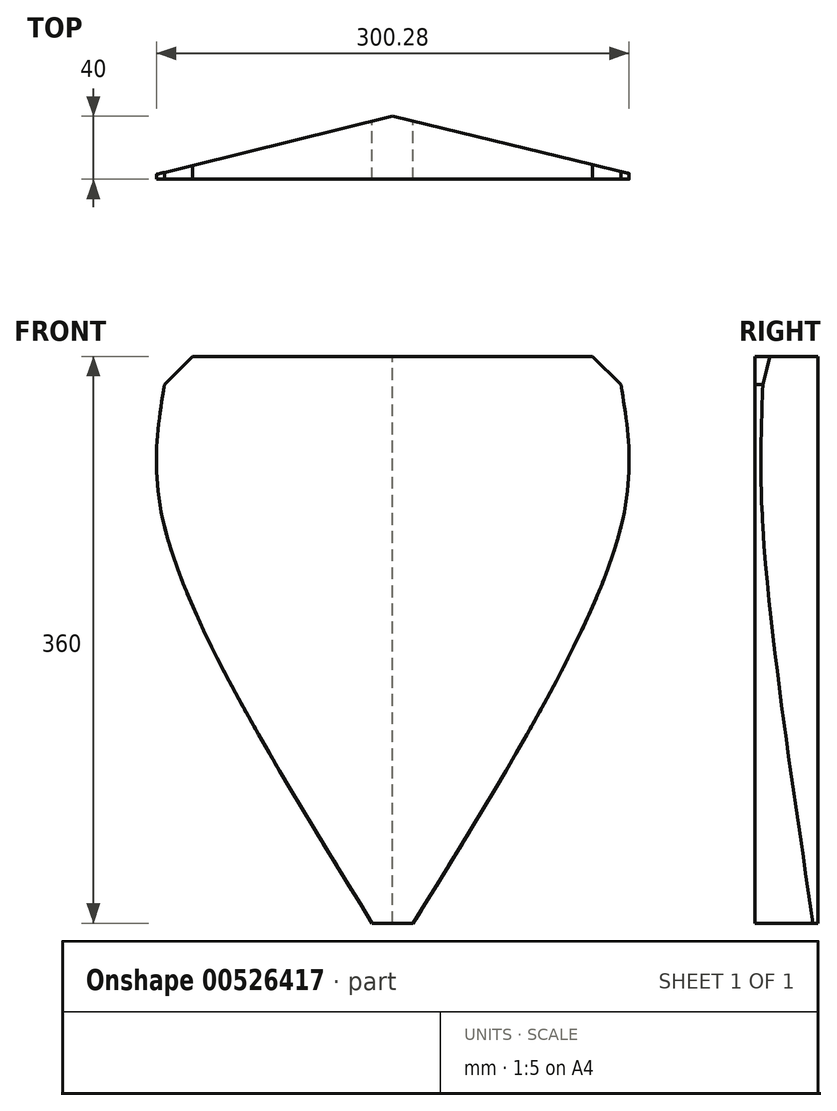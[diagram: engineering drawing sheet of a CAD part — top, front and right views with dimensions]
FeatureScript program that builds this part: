
annotation { "Feature Type Name" : "Feature", "Feature Type Description" : "" }
export const myFeature = defineFeature(function(context is Context, id is Id, definition is map)
    precondition{}
    {
        {
            var Q0;
            Q0=qCreatedBy(makeId("Front.planeOp"),FACE);
            var sketch = newSketch(context, id + "F0", { "sketchPlane" : qUnion([Q0])});
            skLineSegment(sketch, "E0", {"start": v(132, 0) * mm, "end": v(158, 0) * mm});
            skLineSegment(sketch, "E1", {"start": v(0, 252) * mm, "end": v(0, 342) * mm});
            skLineSegment(sketch, "E2", {"start": v(290, 252) * mm, "end": v(290, 342) * mm});
            skLineSegment(sketch, "E3", {"start": v(18, 360) * mm, "end": v(272, 360) * mm});
            skLineSegment(sketch, "E4", {"start": v(18, 360) * mm, "end": v(0, 342) * mm});
            skLineSegment(sketch, "E5", {"start": v(272, 360) * mm, "end": v(290, 342) * mm});
            skLineSegment(sketch, "E6", {"start": v(0, 342) * mm, "end": v(0, 252) * mm});
            skLineSegment(sketch, "E7", {"start": v(290, 342) * mm, "end": v(290, 252) * mm});
            skFitSpline(sketch, "E8", {"points": [v(0, 342) * mm, v(0, 252) * mm, v(132, 0) * mm], "startDerivative": vector(-37.12, -224.14) * mm, "endDerivative": vector(272.25, -439.74) * mm});
            skFitSpline(sketch, "E9", {"points": [v(290, 342) * mm, v(290, 252) * mm, v(158, 0) * mm], "startDerivative": vector(37.12, -224.14) * mm, "endDerivative": vector(-272.25, -439.74) * mm});
            skSolve(sketch);
        }
        {
            var Q0;
            Q0 = qSketchRegion(id + "F0", true);
            extrude(context, id + "F1", {"entities" : qUnion([Q0]), "depth" : 40 * mm, "offsetDistance" : 25 * mm});
        }
        {
            var Q0;
            Q0=makeQuery(id+"F1.opExtrude","SWEPT_FACE",FACE,{"disambiguationData":[OSD([sQuery(id+"F0.wireOp",EDGE,"E3")])]});
            var sketch = newSketch(context, id + "F2", { "sketchPlane" : qUnion([Q0])});
            skLineSegment(sketch, "E10", {"start": v(-17.85, -40) * mm, "end": v(-17.85, 46.46) * mm});
            skLineSegment(sketch, "E11", {"start": v(-17.85, 46.46) * mm, "end": v(307.74, 46.46) * mm});
            skLineSegment(sketch, "E12", {"start": v(307.74, 46.46) * mm, "end": v(310.45, -40) * mm});
            skLineSegment(sketch, "E13", {"start": v(-17.85, -40) * mm, "end": v(145, 0) * mm});
            skLineSegment(sketch, "E14", {"start": v(145, 0) * mm, "end": v(310.45, -40) * mm});
            skPoint(sketch, "E15.start.orphan", {"position": v(18, -40) * mm});
            skSolve(sketch);
        }
        {
            var Q0;
            Q0 = qSketchRegion(id + "F2", true);
            extrude(context, id + "F3", {"entities" : qUnion([Q0]), "operationType" : NewBodyOperationType.REMOVE, "oppositeDirection" : true, "depth" : 494 * mm, "offsetDistance" : 25 * mm});
        }
    });
